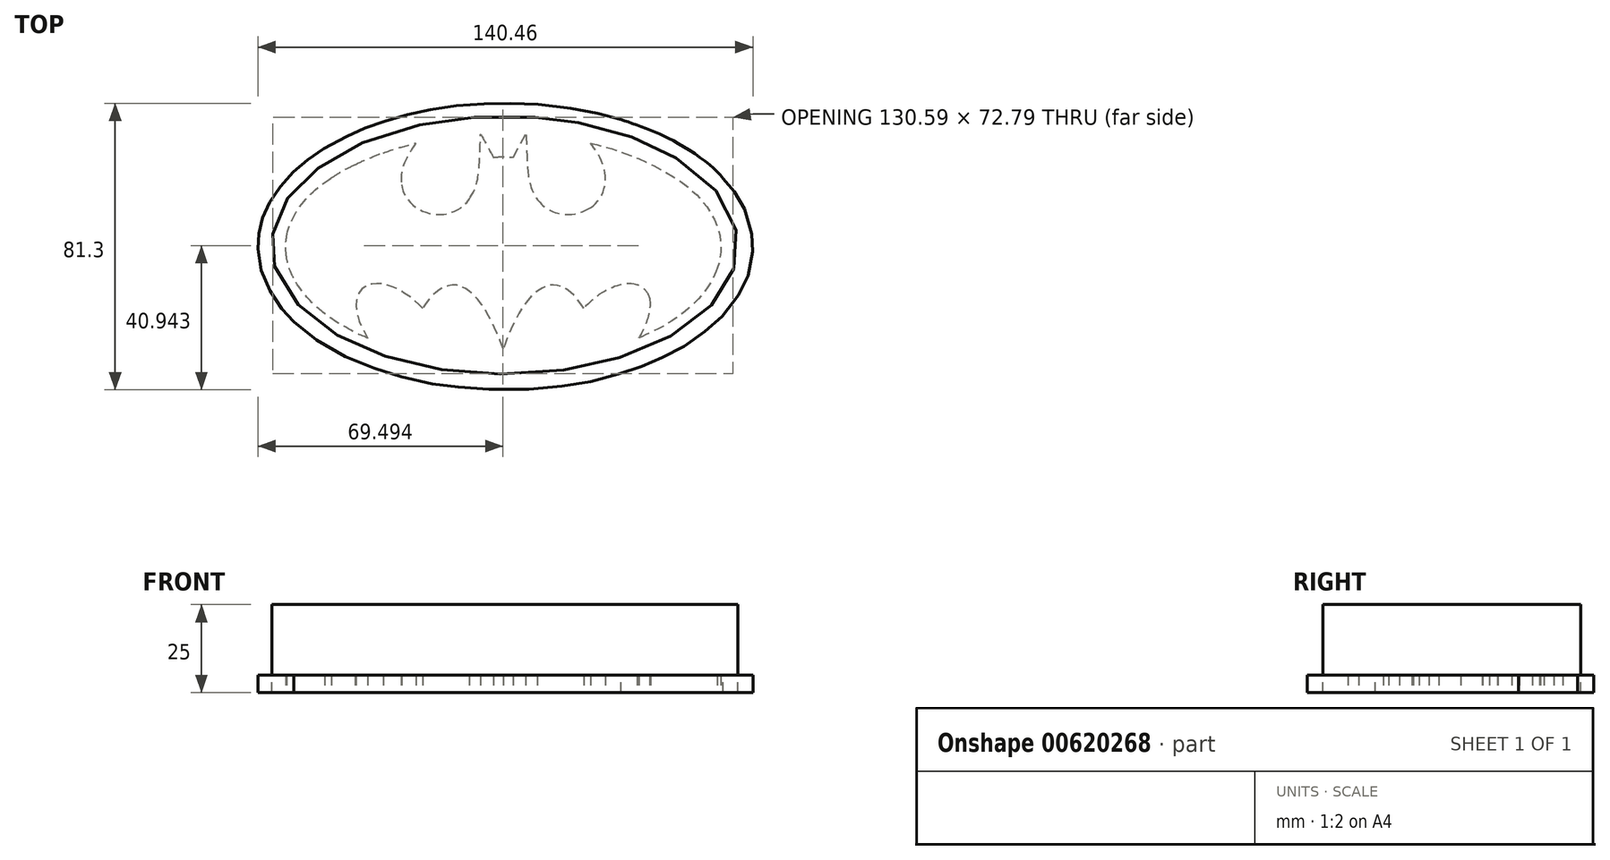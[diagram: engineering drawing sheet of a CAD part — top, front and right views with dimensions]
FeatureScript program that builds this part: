
annotation { "Feature Type Name" : "Feature", "Feature Type Description" : "" }
export const myFeature = defineFeature(function(context is Context, id is Id, definition is map)
    precondition{}
    {
        {
            var Q0;
            Q0=qCreatedBy(makeId("Top.planeOp"),FACE);
            var sketch = newSketch(context, id + "F0", { "sketchPlane" : qUnion([Q0])});
            skFitSpline(sketch, "E0", {"points": [v(34.04, 17.32) * mm, v(32.31, 18.04) * mm, v(30.49, 18.88) * mm, v(26.53, 21.1) * mm, v(24.02, 22.65) * mm, v(22.9, 23.47) * mm, v(21.8, 24.24) * mm], "startDerivative": vector(-11.57, 4.86) * mm, "endDerivative": vector(-8.8, 5.9) * mm});
            skFitSpline(sketch, "E1", {"points": [v(21.8, 24.24) * mm, v(20.84, 25.05) * mm, v(20.34, 25.48) * mm, v(19.68, 26.06) * mm, v(18.96, 26.71) * mm, v(18.24, 27.37) * mm, v(17.08, 28.58) * mm, v(16.4, 29.4) * mm, v(15.8, 30.06) * mm, v(14.55, 31.76) * mm, v(13.73, 33.02) * mm, v(13.33, 33.7) * mm, v(12.95, 34.45) * mm], "startDerivative": vector(-11.84, 9.95) * mm, "endDerivative": vector(-5.13, 10.7) * mm});
            skFitSpline(sketch, "E2", {"points": [v(12.95, 34.45) * mm, v(12.67, 34.96) * mm, v(12.05, 36.43) * mm, v(11.64, 37.48) * mm, v(11.36, 38.47) * mm, v(11.16, 39.2) * mm, v(11.02, 40.03) * mm], "startDerivative": vector(-1.96, 3.25) * mm, "endDerivative": vector(-0.8, 5.55) * mm});
            skFitSpline(sketch, "E3", {"points": [v(11.02, 40.03) * mm, v(10.91, 40.62) * mm, v(10.78, 42.1) * mm, v(10.68, 43.33) * mm, v(11.02, 46.2) * mm], "startDerivative": vector(-0.71, 3.14) * mm, "endDerivative": vector(1.38, 9.1) * mm});
            skFitSpline(sketch, "E4", {"points": [v(11.02, 46.2) * mm, v(11.18, 47.15) * mm, v(11.56, 48.53) * mm, v(12.11, 50.09) * mm, v(13.33, 52.45) * mm, v(14.36, 54.14) * mm, v(15.57, 55.73) * mm, v(16.62, 56.96) * mm, v(18.13, 58.46) * mm, v(19.24, 59.49) * mm, v(21.02, 60.95) * mm, v(22.53, 62.03) * mm, v(23.73, 62.85) * mm], "startDerivative": vector(2.07, 14.7) * mm, "endDerivative": vector(15.5, 10.7) * mm});
            skFitSpline(sketch, "E5", {"points": [v(23.73, 62.85) * mm, v(24.96, 63.65) * mm, v(26.85, 64.76) * mm, v(28.52, 65.67) * mm, v(30.4, 66.57) * mm], "startDerivative": vector(5.21, 3.48) * mm, "endDerivative": vector(7.38, 3.41) * mm});
            skFitSpline(sketch, "E6", {"points": [v(30.4, 66.57) * mm, v(31.56, 67.13) * mm, v(32.91, 67.76) * mm, v(34.52, 68.45) * mm, v(35.93, 69) * mm, v(37.02, 69.43) * mm, v(38.46, 69.9) * mm], "startDerivative": vector(7.27, 3.5) * mm, "endDerivative": vector(8.83, 2.72) * mm});
            skFitSpline(sketch, "E7", {"points": [v(38.46, 69.9) * mm, v(40.92, 70.78) * mm, v(42.66, 71.33) * mm, v(44.64, 71.9) * mm, v(46.6, 72.45) * mm, v(47.74, 72.7) * mm], "startDerivative": vector(11.03, 4.05) * mm, "endDerivative": vector(6.8, 1.35) * mm});
            skFitSpline(sketch, "E8", {"points": [v(47.74, 72.7) * mm, v(47.02, 71.72) * mm, v(45.83, 69.9) * mm, v(45, 68.44) * mm, v(44.2, 66.53) * mm, v(43.75, 65.02) * mm, v(43.49, 62.89) * mm, v(43.63, 60.78) * mm], "startDerivative": vector(-5.72, -7.6) * mm, "endDerivative": vector(1.52, -13.53) * mm});
            skFitSpline(sketch, "E9", {"points": [v(43.63, 60.78) * mm, v(43.73, 60.24) * mm, v(44.14, 58.81) * mm, v(45.12, 56.99) * mm, v(46.39, 55.55) * mm, v(47.48, 54.6) * mm, v(48.81, 53.78) * mm, v(50.07, 53.21) * mm, v(51.25, 52.82) * mm, v(52.5, 52.55) * mm, v(53.88, 52.43) * mm, v(55.27, 52.46) * mm, v(56.96, 52.74) * mm, v(58.15, 53.15) * mm, v(59.35, 53.7) * mm, v(60.58, 54.47) * mm, v(61.75, 55.47) * mm, v(62.8, 56.84) * mm], "startDerivative": vector(2.07, -13.08) * mm, "endDerivative": vector(15.69, 22.34) * mm});
            skFitSpline(sketch, "E10", {"points": [v(62.8, 56.84) * mm, v(63.26, 57.45) * mm, v(64.1, 59.01) * mm, v(64.46, 59.91) * mm, v(64.72, 60.58) * mm, v(65.07, 61.95) * mm, v(65.28, 63.11) * mm, v(65.4, 64.07) * mm, v(65.62, 66.1) * mm, v(65.79, 69.7) * mm, v(65.93, 72.97) * mm, v(66, 74.6) * mm, v(66.02, 75.21) * mm], "startDerivative": vector(6.9, 8.52) * mm, "endDerivative": vector(0.3, 10.1) * mm});
            skFitSpline(sketch, "E11", {"points": [v(66.02, 75.21) * mm, v(66.18, 75.03) * mm, v(66.95, 73.65) * mm, v(67.74, 72.2) * mm, v(68.25, 71.2) * mm, v(69.15, 69.6) * mm, v(69.7, 68.64) * mm], "startDerivative": vector(1.86, -1.67) * mm, "endDerivative": vector(3.2, -5.33) * mm});
            skFitSpline(sketch, "E12", {"points": [v(69.7, 68.64) * mm, v(70.4, 68.73) * mm, v(71.76, 68.8) * mm, v(73.36, 68.8) * mm, v(74.64, 68.74) * mm, v(75.24, 68.64) * mm], "startDerivative": vector(3.92, 0.6) * mm, "endDerivative": vector(3.6, -0.73) * mm});
            skFitSpline(sketch, "E13", {"points": [v(75.24, 68.64) * mm, v(78.85, 75.21) * mm], "startDerivative": vector(3.61, 6.58) * mm, "endDerivative": vector(3.61, 6.58) * mm});
            skFitSpline(sketch, "E14", {"points": [v(78.85, 75.21) * mm, v(78.94, 74.14) * mm, v(79.37, 65.14) * mm, v(79.5, 64.09) * mm, v(79.65, 62.82) * mm, v(79.97, 61.36) * mm, v(80.3, 60.28) * mm, v(80.78, 59.1) * mm, v(81.09, 58.35) * mm, v(81.73, 57.25) * mm, v(82.13, 56.7) * mm], "startDerivative": vector(1, -7.8) * mm, "endDerivative": vector(5.56, -7.14) * mm});
            skFitSpline(sketch, "E15", {"points": [v(82.13, 56.7) * mm, v(82.98, 55.7) * mm, v(84.03, 54.7) * mm, v(85.4, 53.76) * mm, v(87.32, 52.97) * mm, v(89.47, 52.44) * mm, v(92.44, 52.54) * mm, v(94.74, 53.14) * mm, v(97.21, 54.36) * mm], "startDerivative": vector(8.22, -10.15) * mm, "endDerivative": vector(17.33, 9.39) * mm});
            skFitSpline(sketch, "E16", {"points": [v(97.21, 54.36) * mm, v(98.9, 55.78) * mm, v(100.3, 57.79) * mm, v(101.18, 60.33) * mm, v(101.47, 62.22) * mm, v(101.28, 64.35) * mm, v(100.9, 65.94) * mm, v(99.98, 68.3) * mm, v(99.2, 69.87) * mm, v(98.2, 71.3) * mm, v(97.21, 72.65) * mm], "startDerivative": vector(16.99, 12.76) * mm, "endDerivative": vector(-10.99, 14.68) * mm});
            skFitSpline(sketch, "E17", {"points": [v(97.21, 72.65) * mm, v(98.3, 72.43) * mm, v(99.62, 72.06) * mm, v(101.53, 71.57) * mm, v(103.14, 71.1) * mm, v(105.48, 70.32) * mm, v(108.49, 69.2) * mm, v(110.68, 68.32) * mm, v(112.63, 67.46) * mm, v(114.13, 66.79) * mm, v(117.26, 65.2) * mm, v(120.54, 63.29) * mm, v(122.68, 61.85) * mm, v(125.42, 59.72) * mm, v(127.28, 58.02) * mm, v(128.64, 56.57) * mm, v(129.73, 55.24) * mm, v(130.73, 53.8) * mm, v(131.66, 52.34) * mm, v(132.35, 51.03) * mm, v(133.26, 48.84) * mm, v(133.73, 47.23) * mm, v(134.1, 45.21) * mm, v(134.21, 43.42) * mm, v(134.09, 40.94) * mm, v(133.73, 38.97) * mm, v(133.2, 37.23) * mm], "startDerivative": vector(39.07, -6.76) * mm, "endDerivative": vector(-15.72, -48.5) * mm});
            skFitSpline(sketch, "E18", {"points": [v(133.2, 37.23) * mm, v(131.76, 33.92) * mm, v(128.38, 29.14) * mm, v(124.85, 25.68) * mm, v(119.6, 21.75) * mm, v(114.2, 18.9) * mm, v(110.95, 17.36) * mm], "startDerivative": vector(-8.2, -22.39) * mm, "endDerivative": vector(-21.66, -10.13) * mm});
            skFitSpline(sketch, "E19", {"points": [v(110.95, 17.36) * mm, v(111.43, 18.13) * mm, v(112.44, 20.12) * mm, v(113.44, 22.68) * mm, v(114.02, 25.03) * mm, v(114.2, 27.42) * mm, v(113.97, 28.89) * mm], "startDerivative": vector(3.94, 5.96) * mm, "endDerivative": vector(-2.2, 9.4) * mm});
            skFitSpline(sketch, "E20", {"points": [v(113.97, 28.89) * mm, v(113.54, 29.84) * mm, v(112.87, 30.78) * mm, v(111.81, 31.76) * mm, v(110.42, 32.43) * mm], "startDerivative": vector(-1.73, 4.32) * mm, "endDerivative": vector(-5.3, 2.12) * mm});
            skFitSpline(sketch, "E21", {"points": [v(110.42, 32.43) * mm, v(109.68, 32.65) * mm, v(108.22, 32.82) * mm, v(106.66, 32.7) * mm, v(104.84, 32.24) * mm, v(103.19, 31.6) * mm, v(101.2, 30.61) * mm, v(98.61, 28.89) * mm, v(96.79, 27.3) * mm, v(95.34, 25.83) * mm], "startDerivative": vector(-9.38, 3.18) * mm, "endDerivative": vector(-12.09, -12.67) * mm});
            skFitSpline(sketch, "E22", {"points": [v(95.34, 25.83) * mm, v(93.55, 28.25) * mm, v(91.44, 30.41) * mm, v(88.94, 31.98) * mm, v(86.74, 32.43) * mm, v(85.2, 32.2) * mm, v(83.46, 31.55) * mm, v(80.84, 29.64) * mm, v(78.6, 27) * mm, v(75.86, 22.38) * mm, v(73.6, 17.36) * mm, v(72.47, 14.27) * mm], "startDerivative": vector(-19.47, 27.6) * mm, "endDerivative": vector(-10.99, -31.08) * mm});
            skFitSpline(sketch, "E23", {"points": [v(72.47, 14.27) * mm, v(71.78, 15.93) * mm, v(70.58, 18.9) * mm, v(69.1, 22.12) * mm, v(67.42, 25.22) * mm, v(65.45, 28.04) * mm, v(63.29, 30.3) * mm, v(61.9, 31.32) * mm, v(60.2, 32.12) * mm, v(58.3, 32.43) * mm, v(56.76, 32.15) * mm, v(55.48, 31.72) * mm, v(53.83, 30.7) * mm, v(52.32, 29.35) * mm, v(51.12, 27.93) * mm, v(49.55, 25.83) * mm], "startDerivative": vector(-11.01, 26.08) * mm, "endDerivative": vector(-22.92, -31.1) * mm});
            skFitSpline(sketch, "E24", {"points": [v(49.55, 25.83) * mm, v(48.44, 26.87) * mm, v(46.22, 28.89) * mm, v(44.48, 30.04) * mm, v(43.37, 30.8) * mm, v(40.38, 32.15) * mm, v(38.13, 32.69) * mm, v(36.76, 32.77) * mm, v(35.53, 32.71) * mm, v(34.67, 32.58) * mm, v(33.63, 32.1) * mm, v(33.13, 31.85) * mm, v(32.14, 31.02) * mm, v(31.37, 29.92) * mm, v(30.98, 28.77) * mm, v(30.85, 28.37) * mm, v(30.7, 26.77) * mm, v(30.8, 25.22) * mm, v(31.14, 23.6) * mm, v(31.77, 21.76) * mm, v(32.6, 19.86) * mm, v(34.04, 17.32) * mm], "startDerivative": vector(-21.45, 19.82) * mm, "endDerivative": vector(23.93, -40.5) * mm});
            skSolve(sketch);
        }
        {
            var Q0;
            Q0=makeQuery(id+"F0.imprint","IMPRINT",FACE,{"disambiguationData":[TD([[makeQuery(id+"F0.imprint","IMPRINT",EDGE,{"derivedFrom":sQuery(id+"F0.wireOp",EDGE,"E0")}),-1.0]])]});
            extrude(context, id + "F1", {"entities" : qUnion([Q0]), "depth" : 25 * mm, "offsetDistance" : 25 * mm});
        }
        {
            var Q0;
            Q0=makeQuery(id+"F1.opExtrude","CAP_FACE",FACE,{"disambiguationData":[OSD([sQuery(id+"F0.wireOp",EDGE,"E0"),sQuery(id+"F0.wireOp",EDGE,"E1"),sQuery(id+"F0.wireOp",EDGE,"E2"),sQuery(id+"F0.wireOp",EDGE,"E3"),sQuery(id+"F0.wireOp",EDGE,"E4"),sQuery(id+"F0.wireOp",EDGE,"E5"),sQuery(id+"F0.wireOp",EDGE,"E6"),sQuery(id+"F0.wireOp",EDGE,"E7"),sQuery(id+"F0.wireOp",EDGE,"E8"),sQuery(id+"F0.wireOp",EDGE,"E9"),sQuery(id+"F0.wireOp",EDGE,"E10"),sQuery(id+"F0.wireOp",EDGE,"E11"),sQuery(id+"F0.wireOp",EDGE,"E12"),sQuery(id+"F0.wireOp",EDGE,"E13"),sQuery(id+"F0.wireOp",EDGE,"E14"),sQuery(id+"F0.wireOp",EDGE,"E15"),sQuery(id+"F0.wireOp",EDGE,"E16"),sQuery(id+"F0.wireOp",EDGE,"E17"),sQuery(id+"F0.wireOp",EDGE,"E18"),sQuery(id+"F0.wireOp",EDGE,"E19"),sQuery(id+"F0.wireOp",EDGE,"E20"),sQuery(id+"F0.wireOp",EDGE,"E21"),sQuery(id+"F0.wireOp",EDGE,"E22"),sQuery(id+"F0.wireOp",EDGE,"E23"),sQuery(id+"F0.wireOp",EDGE,"E24")])],"isStart":false});
            var sketch = newSketch(context, id + "F2", { "sketchPlane" : qUnion([Q0])});
            skFitSpline(sketch, "E25", {"points": [v(64.2, 80) * mm, v(62.36, 79.91) * mm, v(57.68, 79.4) * mm, v(48.74, 77.89) * mm, v(40.93, 75.77) * mm, v(34.44, 73.53) * mm, v(30.92, 72.05) * mm, v(25.4, 69.22) * mm, v(21.92, 67.04) * mm, v(18.11, 64.24) * mm, v(15.1, 61.5) * mm, v(13.24, 59.55) * mm, v(11.44, 57.28) * mm, v(9.86, 54.74) * mm, v(8.64, 52.36) * mm, v(7.59, 49.37) * mm, v(7, 46.8) * mm, v(6.83, 44.7) * mm, v(6.79, 43.45) * mm, v(6.84, 42.2) * mm, v(7.09, 40.1) * mm, v(7.88, 36.95) * mm, v(9.87, 32.63) * mm, v(11.02, 30.75) * mm, v(13.55, 27.52) * mm, v(16.99, 24.15) * mm, v(20.05, 21.66) * mm, v(24.2, 18.93) * mm, v(28.84, 16.35) * mm, v(33.02, 14.47) * mm, v(37.29, 12.8) * mm, v(46.93, 9.93) * mm, v(50.49, 9.23) * mm, v(55.44, 8.3) * mm, v(62.41, 7.48) * mm, v(66.73, 7.22) * mm, v(75.67, 7.08) * mm, v(80.49, 7.26) * mm, v(89.63, 8.21) * mm, v(95.2, 9.2) * mm, v(101.55, 10.67) * mm, v(107.64, 12.53) * mm, v(112.01, 14.14) * mm, v(118.05, 16.92) * mm, v(122.72, 19.58) * mm, v(127.02, 22.7) * mm, v(130.39, 25.58) * mm, v(133.42, 28.87) * mm, v(135.18, 31.38) * mm, v(137, 34.7) * mm, v(138.06, 37.54) * mm, v(138.66, 39.93) * mm, v(138.98, 43.02) * mm, v(138.84, 46.31) * mm, v(138.33, 48.91) * mm, v(136.84, 53.09) * mm, v(135.22, 55.92) * mm, v(133.1, 58.9) * mm, v(130.58, 61.61) * mm, v(125.82, 65.69) * mm, v(121.9, 68.29) * mm, v(116.53, 71.26) * mm, v(112.6, 72.95) * mm, v(109.7, 74.17) * mm, v(104.25, 75.98) * mm, v(98.55, 77.49) * mm, v(93.67, 78.5) * mm, v(89.7, 79.16) * mm, v(85.72, 79.66) * mm, v(82.78, 79.94) * mm, v(78.16, 80.28) * mm, v(67.97, 80.23) * mm, v(64.2, 80) * mm]});
            skSolve(sketch);
        }
        {
            var Q0;
            Q0=makeQuery(id+"F2.imprint","IMPRINT",FACE,{"disambiguationData":[TD([[makeQuery(id+"F2.imprint","IMPRINT",EDGE,{"derivedFrom":sQuery(id+"F2.wireOp",EDGE,"E25")}),1.0]])]});
            extrude(context, id + "F3", {"entities" : qUnion([Q0]), "operationType" : NewBodyOperationType.ADD, "oppositeDirection" : true, "depth" : 20 * mm, "offsetDistance" : 25 * mm});
        }
        {
            var Q0;
            Q0=makeQuery(id+"F3.opExtrude","CAP_FACE",FACE,{"disambiguationData":[OSD([sQuery(id+"F0.wireOp",EDGE,"E0"),sQuery(id+"F0.wireOp",EDGE,"E1"),sQuery(id+"F0.wireOp",EDGE,"E2"),sQuery(id+"F0.wireOp",EDGE,"E3"),sQuery(id+"F0.wireOp",EDGE,"E4"),sQuery(id+"F0.wireOp",EDGE,"E5"),sQuery(id+"F0.wireOp",EDGE,"E6"),sQuery(id+"F0.wireOp",EDGE,"E7"),sQuery(id+"F0.wireOp",EDGE,"E8"),sQuery(id+"F0.wireOp",EDGE,"E9"),sQuery(id+"F0.wireOp",EDGE,"E10"),sQuery(id+"F0.wireOp",EDGE,"E11"),sQuery(id+"F0.wireOp",EDGE,"E12"),sQuery(id+"F0.wireOp",EDGE,"E13"),sQuery(id+"F0.wireOp",EDGE,"E14"),sQuery(id+"F0.wireOp",EDGE,"E15"),sQuery(id+"F0.wireOp",EDGE,"E16"),sQuery(id+"F0.wireOp",EDGE,"E17"),sQuery(id+"F0.wireOp",EDGE,"E18"),sQuery(id+"F0.wireOp",EDGE,"E19"),sQuery(id+"F0.wireOp",EDGE,"E20"),sQuery(id+"F0.wireOp",EDGE,"E21"),sQuery(id+"F0.wireOp",EDGE,"E22"),sQuery(id+"F0.wireOp",EDGE,"E23"),sQuery(id+"F0.wireOp",EDGE,"E24"),sQuery(id+"F2.wireOp",EDGE,"E25")])],"isStart":false});
            var sketch = newSketch(context, id + "F4", { "sketchPlane" : qUnion([Q0])});
            skFitSpline(sketch, "E26", {"points": [v(105.83, -79.38) * mm, v(102.74, -80.23) * mm, v(95.93, -81.82) * mm, v(91.2, -82.64) * mm, v(82.47, -83.64) * mm, v(75.97, -83.96) * mm, v(71.33, -83.94) * mm, v(65.1, -83.73) * mm, v(59.25, -83.28) * mm, v(53.28, -82.4) * mm, v(49.94, -81.77) * mm, v(45.3, -80.71) * mm, v(40.65, -79.43) * mm, v(37.04, -78.3) * mm, v(33.9, -77.19) * mm, v(31.16, -76.06) * mm, v(28.2, -74.7) * mm, v(23.54, -72.3) * mm, v(19.68, -69.9) * mm, v(17.57, -68.45) * mm, v(15.49, -66.77) * mm, v(13.41, -64.99) * mm, v(11.54, -63.08) * mm, v(9.45, -60.69) * mm, v(7.56, -58.21) * mm, v(6.16, -55.86) * mm, v(5.26, -54.07) * mm, v(4.3, -51.77) * mm, v(3.56, -49.17) * mm, v(3.18, -47.39) * mm, v(3, -46.38) * mm, v(2.87, -44.92) * mm, v(2.85, -42.37) * mm, v(3.2, -39.1) * mm, v(4.28, -34.9) * mm, v(5.82, -31.46) * mm, v(8.2, -27.51) * mm, v(9.73, -25.57) * mm, v(11.11, -23.96) * mm, v(13.05, -22.03) * mm], "startDerivative": vector(-110.75, -31.66) * mm, "endDerivative": vector(91.13, 87.47) * mm});
            skFitSpline(sketch, "E27", {"points": [v(105.83, -79.38) * mm, v(109.05, -78.3) * mm, v(113.86, -76.49) * mm, v(118.48, -74.5) * mm, v(124.88, -70.92) * mm, v(131.63, -66) * mm, v(134.8, -62.68) * mm], "startDerivative": vector(23.28, 7.56) * mm, "endDerivative": vector(18.15, 21.1) * mm});
            skFitSpline(sketch, "E28", {"points": [v(134.8, -62.68) * mm, v(135.73, -61.86) * mm, v(138.16, -58.65) * mm, v(139.98, -55.65) * mm, v(142.04, -51.26) * mm, v(143.1, -45.53) * mm, v(143.28, -43.62) * mm, v(142.88, -38.8) * mm, v(141.46, -34.02) * mm, v(139.66, -30.3) * mm, v(135.8, -24.9) * mm, v(132.18, -21.22) * mm, v(128.26, -18.08) * mm, v(123.26, -14.72) * mm, v(118.15, -12.1) * mm, v(114.47, -10.35) * mm, v(109.31, -8.41) * mm, v(104.1, -6.8) * mm, v(96.53, -4.86) * mm, v(89.03, -3.7) * mm, v(78.71, -2.75) * mm, v(65.11, -2.95) * mm, v(58.16, -3.58) * mm, v(51.6, -4.51) * mm, v(42.63, -6.61) * mm, v(35.83, -8.77) * mm, v(27.6, -12.16) * mm, v(18.99, -17.17) * mm, v(13.05, -22.03) * mm], "startDerivative": vector(51.17, 38.65) * mm, "endDerivative": vector(-137.02, -121.22) * mm});
            skSolve(sketch);
        }
        {
            var Q0;
            Q0=makeQuery(id+"F4.imprint","IMPRINT",FACE,{"disambiguationData":[TD([[makeQuery(id+"F4.imprint","IMPRINT",EDGE,{"derivedFrom":sQuery(id+"F4.wireOp",EDGE,"E26")}),-1.0]])]});
            extrude(context, id + "F5", {"entities" : qUnion([Q0]), "depth" : 5 * mm, "offsetDistance" : 25 * mm});
        }
    });
